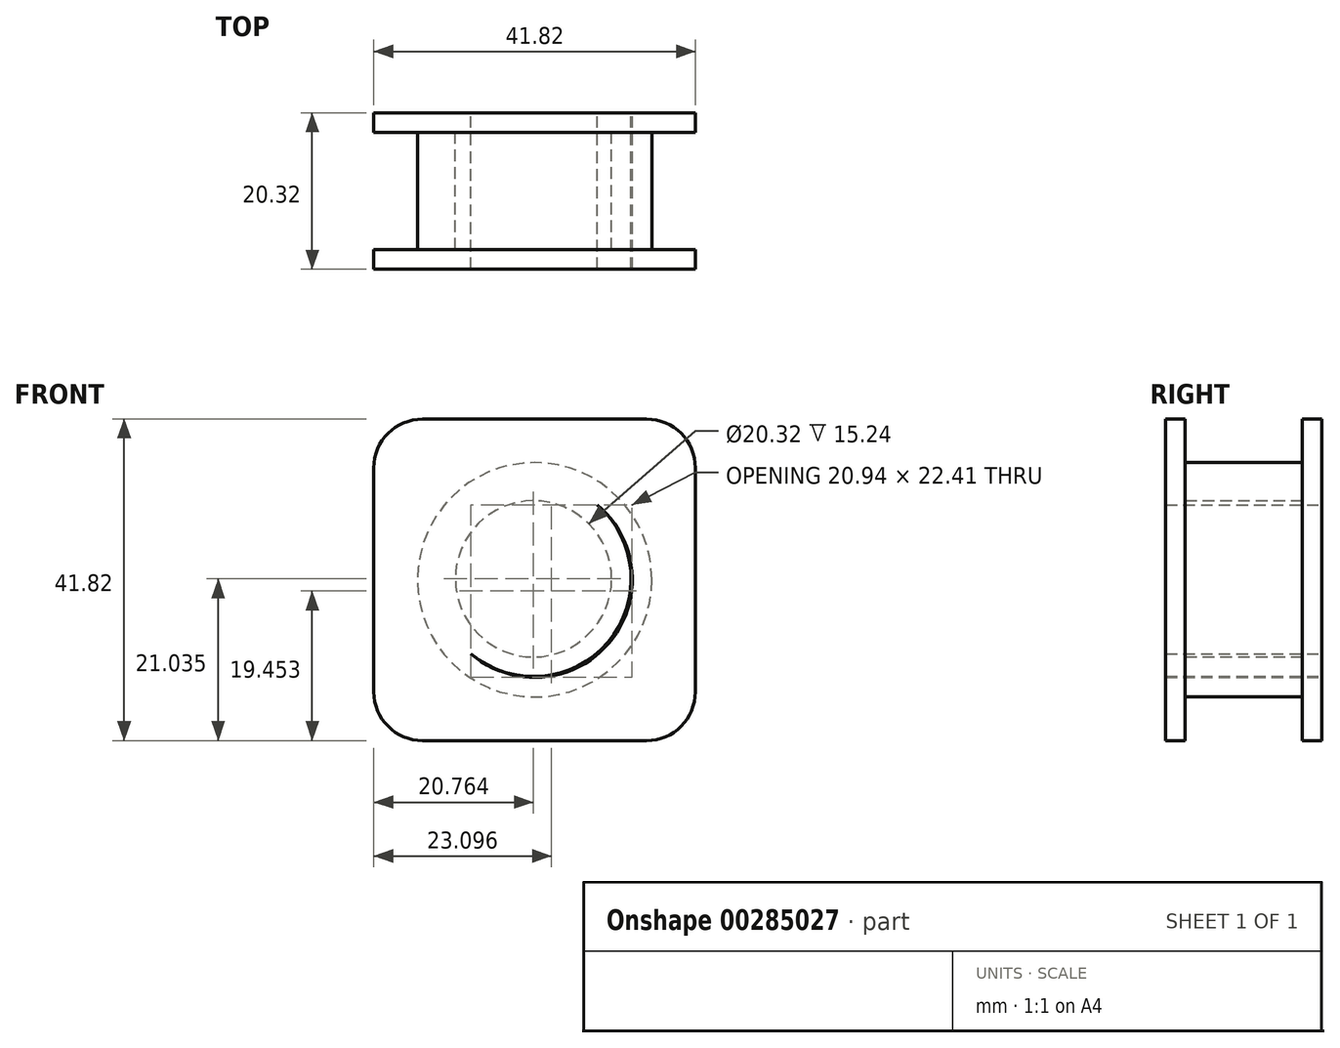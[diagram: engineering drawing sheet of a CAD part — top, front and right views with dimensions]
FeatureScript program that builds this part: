
annotation { "Feature Type Name" : "Feature", "Feature Type Description" : "" }
export const myFeature = defineFeature(function(context is Context, id is Id, definition is map)
    precondition{}
    {
        {
            var Q0;
            Q0=qCreatedBy(makeId("Front.planeOp"),FACE);
            var sketch = newSketch(context, id + "F0", { "sketchPlane" : qUnion([Q0])});
            skLineSegment(sketch, "E0.bottom", {"start": v(-55.4, -15.93) * mm, "end": v(-26.28, -15.93) * mm});
            skLineSegment(sketch, "E0.top", {"start": v(-55.4, 25.89) * mm, "end": v(-26.28, 25.89) * mm});
            skLineSegment(sketch, "E0.left", {"start": v(-61.75, -9.58) * mm, "end": v(-61.75, 19.54) * mm});
            skLineSegment(sketch, "E0.right", {"start": v(-19.93, -9.58) * mm, "end": v(-19.93, 19.54) * mm});
            skCircle(sketch, "E1", {"center": v(-40.84, 4.98) * mm, "radius": 12.7 * mm});
            skPoint(sketch, "E2.visualSharp", {"position": v(-61.75, 25.89) * mm});
            skArc(sketch, "E2.filletArc", {"start": v(-55.4, 25.89) * mm, "mid": v(-59.89, 24.03) * mm, "end": v(-61.75, 19.54) * mm});
            skPoint(sketch, "E3.visualSharp", {"position": v(-19.93, 25.89) * mm});
            skArc(sketch, "E3.filletArc", {"start": v(-19.93, 19.54) * mm, "mid": v(-21.79, 24.03) * mm, "end": v(-26.28, 25.89) * mm});
            skPoint(sketch, "E4.visualSharp", {"position": v(-19.93, -15.93) * mm});
            skArc(sketch, "E4.filletArc", {"start": v(-26.28, -15.93) * mm, "mid": v(-21.79, -14.07) * mm, "end": v(-19.93, -9.58) * mm});
            skPoint(sketch, "E5.visualSharp", {"position": v(-61.75, -15.93) * mm});
            skArc(sketch, "E5.filletArc", {"start": v(-61.75, -9.58) * mm, "mid": v(-59.89, -14.07) * mm, "end": v(-55.4, -15.93) * mm});
            skSolve(sketch);
        }
        {
            var Q0;
            Q0 = qSketchRegion(id + "F0", true);
            extrude(context, id + "F1", {"entities" : qUnion([Q0]), "depth" : 20.32 * mm});
        }
        {
            var Q0;
            Q0=qCreatedBy(makeId("Front.planeOp"),FACE);
            var sketch = newSketch(context, id + "F2", { "sketchPlane" : qUnion([Q0])});
            skCircle(sketch, "E6", {"center": v(-40.99, 5.1) * mm, "radius": 12.7 * mm});
            skSolve(sketch);
        }
        {
            var Q0;
            Q0 = qSketchRegion(id + "F2", true);
            extrude(context, id + "F3", {"entities" : qUnion([Q0]), "operationType" : NewBodyOperationType.ADD, "depth" : 20.32 * mm});
        }
        {
            var Q0;
            Q0=makeQuery(id+"F1.opExtrude","SWEPT_FACE",FACE,{"disambiguationData":[OSD([sQuery(id+"F0.wireOp",EDGE,"E0.top")])]});
            var Q1;
            Q1=makeQuery(id+"F1.opExtrude","SWEPT_FACE",FACE,{"disambiguationData":[OSD([sQuery(id+"F0.wireOp",EDGE,"E0.right")])]});
            var Q2;
            Q2=makeQuery(id+"F1.opExtrude","SWEPT_FACE",FACE,{"disambiguationData":[OSD([sQuery(id+"F0.wireOp",EDGE,"E0.left")])]});
            var Q3;
            Q3=makeQuery(id+"F1.opExtrude","SWEPT_FACE",FACE,{"disambiguationData":[OSD([sQuery(id+"F0.wireOp",EDGE,"E0.bottom")])]});
            var Q4;
            Q4=makeQuery(id+"F1.opExtrude","SWEPT_FACE",FACE,{"disambiguationData":[OSD([sQuery(id+"F0.wireOp",EDGE,"E5.filletArc")])]});
            var Q5;
            Q5=makeQuery(id+"F1.opExtrude","SWEPT_FACE",FACE,{"disambiguationData":[OSD([sQuery(id+"F0.wireOp",EDGE,"E2.filletArc")])]});
            var Q6;
            Q6=makeQuery(id+"F1.opExtrude","SWEPT_FACE",FACE,{"disambiguationData":[OSD([sQuery(id+"F0.wireOp",EDGE,"E3.filletArc")])]});
            var Q7;
            Q7=makeQuery(id+"F1.opExtrude","SWEPT_FACE",FACE,{"disambiguationData":[OSD([sQuery(id+"F0.wireOp",EDGE,"E4.filletArc")])]});
            shell(context, id + "F4", {"entities" : qUnion([Q0, Q1, Q2, Q3, Q4, Q5, Q6, Q7]), "thickness" : 2.54 * mm});
        }
    });
